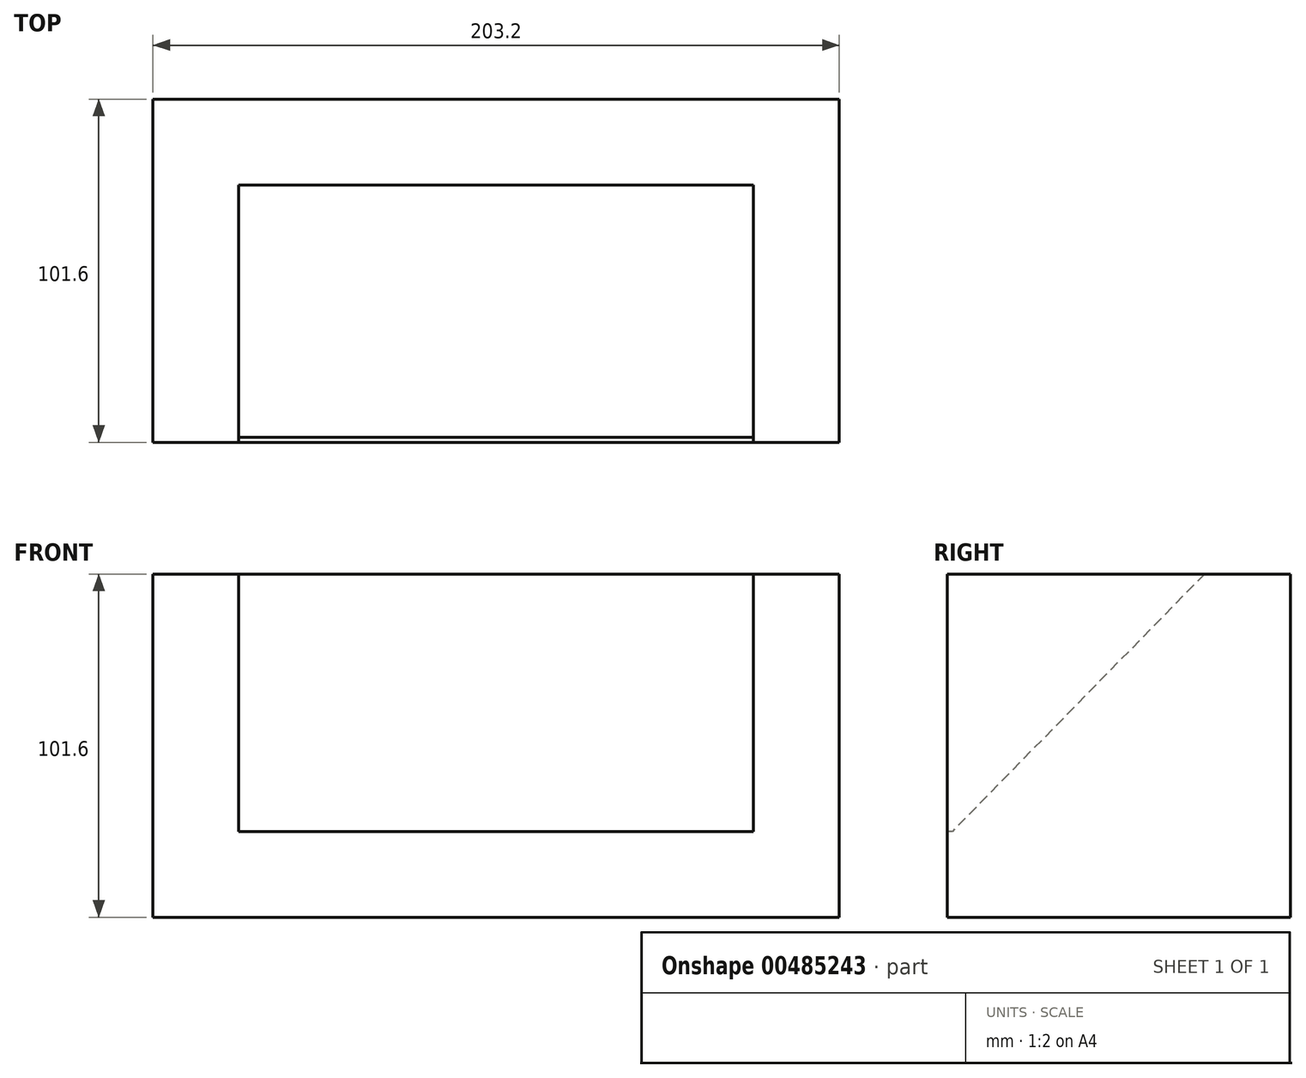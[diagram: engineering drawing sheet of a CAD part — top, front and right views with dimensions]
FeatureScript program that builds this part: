
annotation { "Feature Type Name" : "Feature", "Feature Type Description" : "" }
export const myFeature = defineFeature(function(context is Context, id is Id, definition is map)
    precondition{}
    {
        {
            var Q0;
            Q0=qCreatedBy(makeId("Front.planeOp"),FACE);
            var sketch = newSketch(context, id + "F0", { "sketchPlane" : qUnion([Q0])});
            skLineSegment(sketch, "E0.bottom", {"start": v(-104.94, 64.22) * mm, "end": v(98.26, 64.22) * mm});
            skLineSegment(sketch, "E0.top", {"start": v(-104.94, -37.38) * mm, "end": v(98.26, -37.38) * mm});
            skLineSegment(sketch, "E0.left", {"start": v(-104.94, 64.22) * mm, "end": v(-104.94, -37.38) * mm});
            skLineSegment(sketch, "E0.right", {"start": v(98.26, 64.22) * mm, "end": v(98.26, -37.38) * mm});
            skSolve(sketch);
        }
        {
            var Q0;
            Q0=makeQuery(id+"F0.imprint","IMPRINT",FACE,{"disambiguationData":[TD([[makeQuery(id+"F0.imprint","IMPRINT",EDGE,{"derivedFrom":sQuery(id+"F0.wireOp",EDGE,"E0.bottom")}),-1.0]])]});
            extrude(context, id + "F1", {"entities" : qUnion([Q0]), "depth" : 101.6 * mm});
        }
        {
            var Q0;
            Q0=makeQuery(id+"F1.opExtrude","CAP_FACE",FACE,{"disambiguationData":[OSD([sQuery(id+"F0.wireOp",EDGE,"E0.bottom"),sQuery(id+"F0.wireOp",EDGE,"E0.top"),sQuery(id+"F0.wireOp",EDGE,"E0.left"),sQuery(id+"F0.wireOp",EDGE,"E0.right")])],"isStart":false});
            var sketch = newSketch(context, id + "F2", { "sketchPlane" : qUnion([Q0])});
            skLineSegment(sketch, "E1.bottom", {"start": v(-79.54, 64.22) * mm, "end": v(72.86, 64.22) * mm});
            skLineSegment(sketch, "E1.top", {"start": v(-79.54, -11.98) * mm, "end": v(72.86, -11.98) * mm});
            skLineSegment(sketch, "E1.left", {"start": v(-79.54, 64.22) * mm, "end": v(-79.54, -11.98) * mm});
            skLineSegment(sketch, "E1.right", {"start": v(72.86, 64.22) * mm, "end": v(72.86, -11.98) * mm});
            skSolve(sketch);
        }
        {
            var Q0;
            Q0=makeQuery(id+"F2.imprint","IMPRINT",FACE,{"disambiguationData":[TD([[makeQuery(id+"F2.imprint","IMPRINT",EDGE,{"derivedFrom":sQuery(id+"F2.wireOp",EDGE,"E1.bottom")}),-1.0]])]});
            extrude(context, id + "F3", {"entities" : qUnion([Q0]), "operationType" : NewBodyOperationType.REMOVE, "oppositeDirection" : true, "depth" : 76.2 * mm});
        }
        {
            var Q0;
            Q0=makeQuery(id+"F3.boolean.opBoolean","COPY",FACE,{"derivedFrom":makeQuery(id+"F3.opExtrude","SWEPT_FACE",FACE,{"disambiguationData":[OSD([sQuery(id+"F2.wireOp",EDGE,"E1.left")])]})});
            var sketch = newSketch(context, id + "F4", { "sketchPlane" : qUnion([Q0])});
            skLineSegment(sketch, "E2", {"start": v(-25.4, 64.22) * mm, "end": v(-100.13, -11.98) * mm});
            skLineSegment(sketch, "E3", {"start": v(-100.13, -11.98) * mm, "end": v(-25.4, -11.98) * mm});
            skLineSegment(sketch, "E4", {"start": v(-25.4, -11.98) * mm, "end": v(-25.4, 64.22) * mm});
            skSolve(sketch);
        }
        {
            var Q0;
            Q0 = qSketchRegion(id + "F4", true);
            extrude(context, id + "F5", {"entities" : qUnion([Q0]), "operationType" : NewBodyOperationType.ADD, "depth" : 152.4 * mm});
        }
    });
